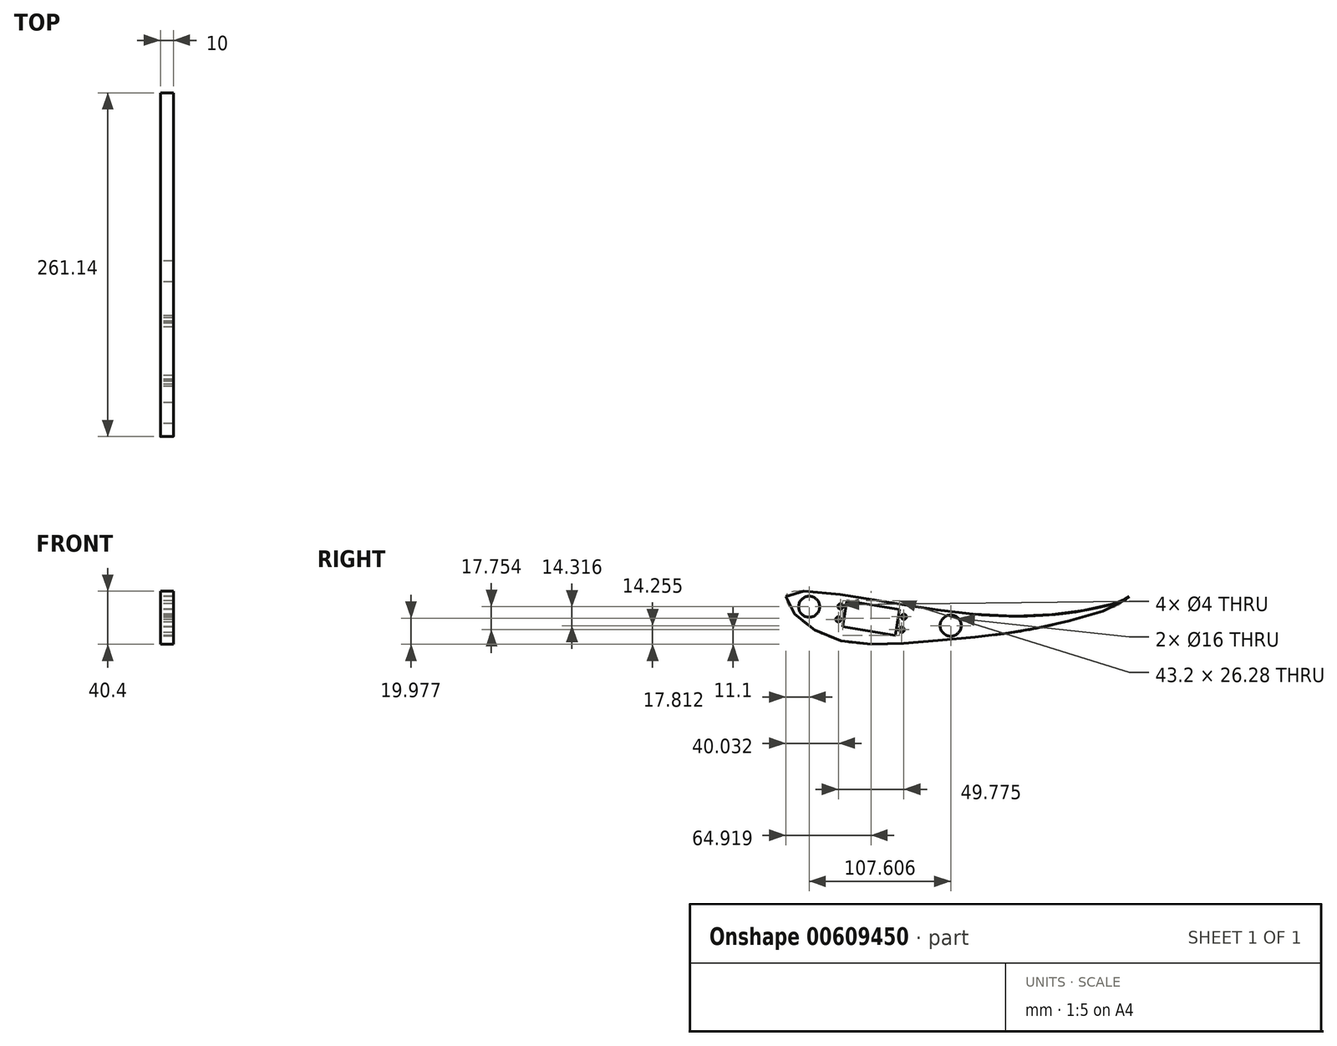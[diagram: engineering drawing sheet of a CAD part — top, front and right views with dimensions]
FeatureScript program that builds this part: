
annotation { "Feature Type Name" : "Feature", "Feature Type Description" : "" }
export const myFeature = defineFeature(function(context is Context, id is Id, definition is map)
    precondition{}
    {
        {
            var Q0;
            Q0=qCreatedBy(makeId("Right.planeOp"),FACE);
            var sketch = newSketch(context, id + "F0", { "sketchPlane" : qUnion([Q0])});
            skFitSpline(sketch, "E0", {"points": [v(-82.9, 15.31) * mm, v(-82.72, 13.45) * mm, v(-81.93, 10.89) * mm, v(-80.76, 8.46) * mm, v(-78.77, 5.4) * mm, v(-76.46, 2.43) * mm, v(-74.09, 0.05) * mm, v(-71.02, -2.74) * mm, v(-66.36, -6.45) * mm, v(-62.04, -9.39) * mm, v(-56.67, -12.3) * mm, v(-51.53, -14.76) * mm, v(-44.09, -17.33) * mm, v(-39.83, -18.56) * mm, v(-32.87, -19.86) * mm, v(-27.68, -20.5) * mm, v(-20.48, -21.04) * mm, v(-10.15, -21.04) * mm, v(-4.84, -20.82) * mm, v(2.75, -20.53) * mm, v(12.43, -19.83) * mm, v(19.42, -19.31) * mm, v(27.83, -18.65) * mm, v(39.73, -17.7) * mm, v(49.58, -16.82) * mm, v(59.18, -15.88) * mm, v(70.48, -14.64) * mm, v(77.85, -13.71) * mm, v(85.2, -12.7) * mm, v(92.53, -11.55) * mm, v(97.88, -10.6) * mm, v(104.42, -9.42) * mm, v(110.6, -8.26) * mm, v(116.81, -6.9) * mm, v(123.02, -5.5) * mm, v(131.68, -3.53) * mm, v(138.5, -1.66) * mm, v(148.52, 1.07) * mm, v(159.76, 4.77) * mm, v(166.04, 7.2) * mm, v(170, 9.1) * mm, v(173.56, 11.24) * mm, v(176.2, 13.38) * mm, v(178.2, 15.16) * mm, v(175.24, 13.46) * mm, v(172.23, 12.09) * mm, v(167.34, 10.21) * mm, v(162.56, 8.66) * mm, v(157.84, 7.47) * mm, v(151.53, 6.06) * mm, v(144.02, 4.71) * mm, v(136.8, 3.42) * mm, v(129.62, 2.55) * mm, v(120.29, 1.49) * mm, v(113.26, 1.09) * mm, v(103.2, 0.48) * mm, v(89.6, 0.4) * mm, v(72.19, 0.9) * mm, v(62.19, 1.65) * mm, v(56.7, 2.08) * mm, v(49.82, 2.85) * mm, v(42.61, 3.72) * mm, v(30.76, 5.31) * mm, v(22.33, 6.5) * mm, v(15.3, 7.74) * mm, v(6.4, 9.02) * mm, v(-0.72, 10.25) * mm, v(-8.45, 11.51) * mm, v(-18.15, 13.11) * mm, v(-26.18, 14.43) * mm, v(-35.39, 15.88) * mm, v(-43.7, 16.98) * mm, v(-53.58, 18.04) * mm, v(-64.74, 18.86) * mm, v(-72.87, 19.27) * mm, v(-77.52, 18.92) * mm, v(-79.16, 18.77) * mm, v(-80.9, 18.34) * mm, v(-81.94, 17.48) * mm, v(-82.9, 15.31) * mm]});
            skPoint(sketch, "E1", {"position": v(-65.13, 7.45) * mm});
            skCircle(sketch, "E2", {"center": v(-65.13, 7.45) * mm, "radius": 8 * mm});
            skPoint(sketch, "E3", {"position": v(42.48, -6.86) * mm});
            skCircle(sketch, "E4", {"center": v(42.48, -6.86) * mm, "radius": 8 * mm});
            skLineSegment(sketch, "E5", {"start": v(-36.39, 12) * mm, "end": v(3.58, 5.45) * mm});
            skLineSegment(sketch, "E6", {"start": v(3.58, 5.45) * mm, "end": v(0.35, -14.28) * mm});
            skLineSegment(sketch, "E7", {"start": v(0.35, -14.28) * mm, "end": v(-39.62, -7.74) * mm});
            skLineSegment(sketch, "E8", {"start": v(-39.62, -7.74) * mm, "end": v(-36.39, 12) * mm});
            skPoint(sketch, "E9", {"position": v(6.87, -0.15) * mm});
            skPoint(sketch, "E10", {"position": v(5.25, -10.02) * mm});
            skPoint(sketch, "E11", {"position": v(-41.3, 7.73) * mm});
            skPoint(sketch, "E12", {"position": v(-42.9, -2.13) * mm});
            skCircle(sketch, "E13", {"center": v(-41.3, 7.73) * mm, "radius": 2 * mm});
            skCircle(sketch, "E14", {"center": v(-42.9, -2.13) * mm, "radius": 2 * mm});
            skCircle(sketch, "E15", {"center": v(6.87, -0.15) * mm, "radius": 2 * mm});
            skCircle(sketch, "E16", {"center": v(5.25, -10.02) * mm, "radius": 2 * mm});
            skSolve(sketch);
        }
        {
            var Q0;
            Q0=makeQuery(id+"F0.imprint","IMPRINT",FACE,{"disambiguationData":[TD([[makeQuery(id+"F0.imprint","IMPRINT",EDGE,{"derivedFrom":sQuery(id+"F0.wireOp",EDGE,"E0")}),1.0]])]});
            extrude(context, id + "F1", {"entities" : qUnion([Q0]), "depth" : 10 * mm, "offsetDistance" : 25.4 * mm});
        }
    });
